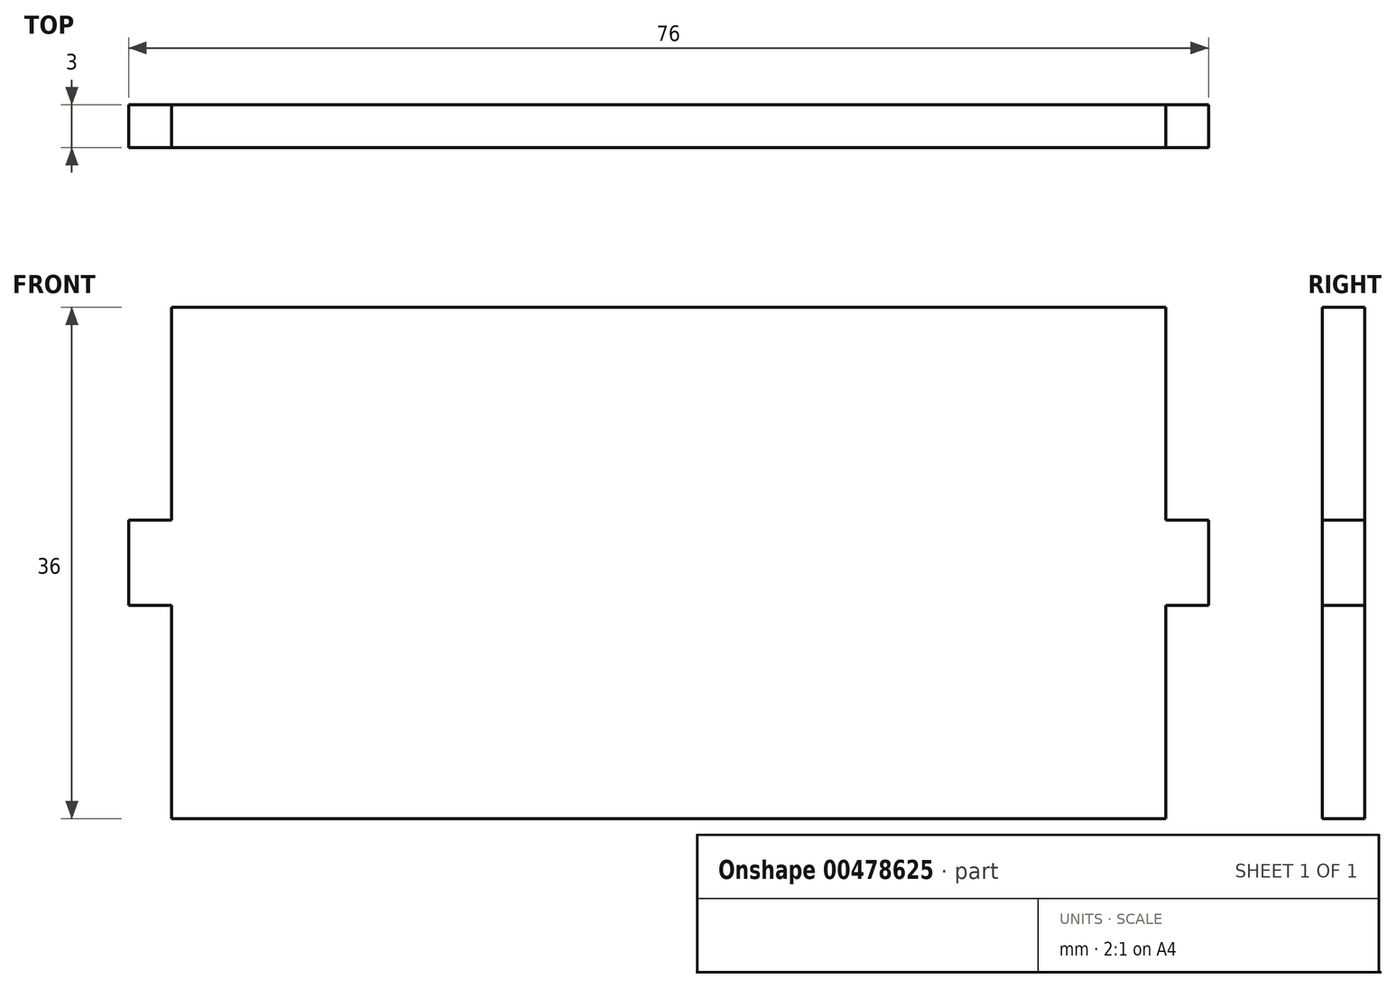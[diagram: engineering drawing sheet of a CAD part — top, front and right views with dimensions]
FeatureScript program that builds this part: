
annotation { "Feature Type Name" : "Feature", "Feature Type Description" : "" }
export const myFeature = defineFeature(function(context is Context, id is Id, definition is map)
    precondition{}
    {
        {
            var Q0;
            Q0=qCreatedBy(makeId("Front.planeOp"),FACE);
            var sketch = newSketch(context, id + "F0", { "sketchPlane" : qUnion([Q0])});
            skLineSegment(sketch, "E0.bottom", {"start": v(35, 18) * mm, "end": v(-35, 18) * mm});
            skLineSegment(sketch, "E0.top", {"start": v(35, -18) * mm, "end": v(-35, -18) * mm});
            skLineSegment(sketch, "E0.left", {"start": v(35, 18) * mm, "end": v(35, -18) * mm});
            skLineSegment(sketch, "E0.right", {"start": v(-35, 18) * mm, "end": v(-35, -18) * mm});
            skPoint(sketch, "E0.middle", {"position": v(0, 0) * mm});
            skSolve(sketch);
        }
        {
            var Q0;
            Q0 = qSketchRegion(id + "F0", true);
            extrude(context, id + "F1", {"entities" : qUnion([Q0]), "depth" : 3 * mm});
        }
        {
            var Q0;
            Q0=makeQuery(id+"F1.opExtrude","CAP_FACE",FACE,{"disambiguationData":[OSD([sQuery(id+"F0.wireOp",EDGE,"E0.bottom"),sQuery(id+"F0.wireOp",EDGE,"E0.top"),sQuery(id+"F0.wireOp",EDGE,"E0.left"),sQuery(id+"F0.wireOp",EDGE,"E0.right")])],"isStart":false});
            var sketch = newSketch(context, id + "F2", { "sketchPlane" : qUnion([Q0])});
            skLineSegment(sketch, "E1", {"start": v(-35, 0) * mm, "end": v(-38, 0) * mm, "construction": true});
            skPoint(sketch, "E1.endSnap0", {"position": v(-35, 0) * mm});
            skLineSegment(sketch, "E2.bottom", {"start": v(-35, 3) * mm, "end": v(-38, 3) * mm});
            skLineSegment(sketch, "E2.top", {"start": v(-35, -3) * mm, "end": v(-38, -3) * mm});
            skLineSegment(sketch, "E2.left", {"start": v(-35, 3) * mm, "end": v(-35, -3) * mm});
            skLineSegment(sketch, "E2.right", {"start": v(-38, 3) * mm, "end": v(-38, -3) * mm});
            skPoint(sketch, "E2.middle", {"position": v(-36.5, 0) * mm});
            skLineSegment(sketch, "E3", {"start": v(0, 18) * mm, "end": v(0, 11.26) * mm, "construction": true});
            skPoint(sketch, "E3.endSnap0", {"position": v(0, 18) * mm});
            skLineSegment(sketch, "E4.MirrorCS", {"start": v(35, 3) * mm, "end": v(38, 3) * mm});
            skLineSegment(sketch, "E5.MirrorCS", {"start": v(35, 3) * mm, "end": v(35, -3) * mm});
            skLineSegment(sketch, "E6.MirrorCS", {"start": v(38, 3) * mm, "end": v(38, -3) * mm});
            skLineSegment(sketch, "E7.MirrorCS", {"start": v(35, -3) * mm, "end": v(38, -3) * mm});
            skSolve(sketch);
        }
        {
            var Q0;
            Q0 = qSketchRegion(id + "F2", true);
            extrude(context, id + "F3", {"entities" : qUnion([Q0]), "operationType" : NewBodyOperationType.ADD, "oppositeDirection" : true, "depth" : 3 * mm});
        }
    });
